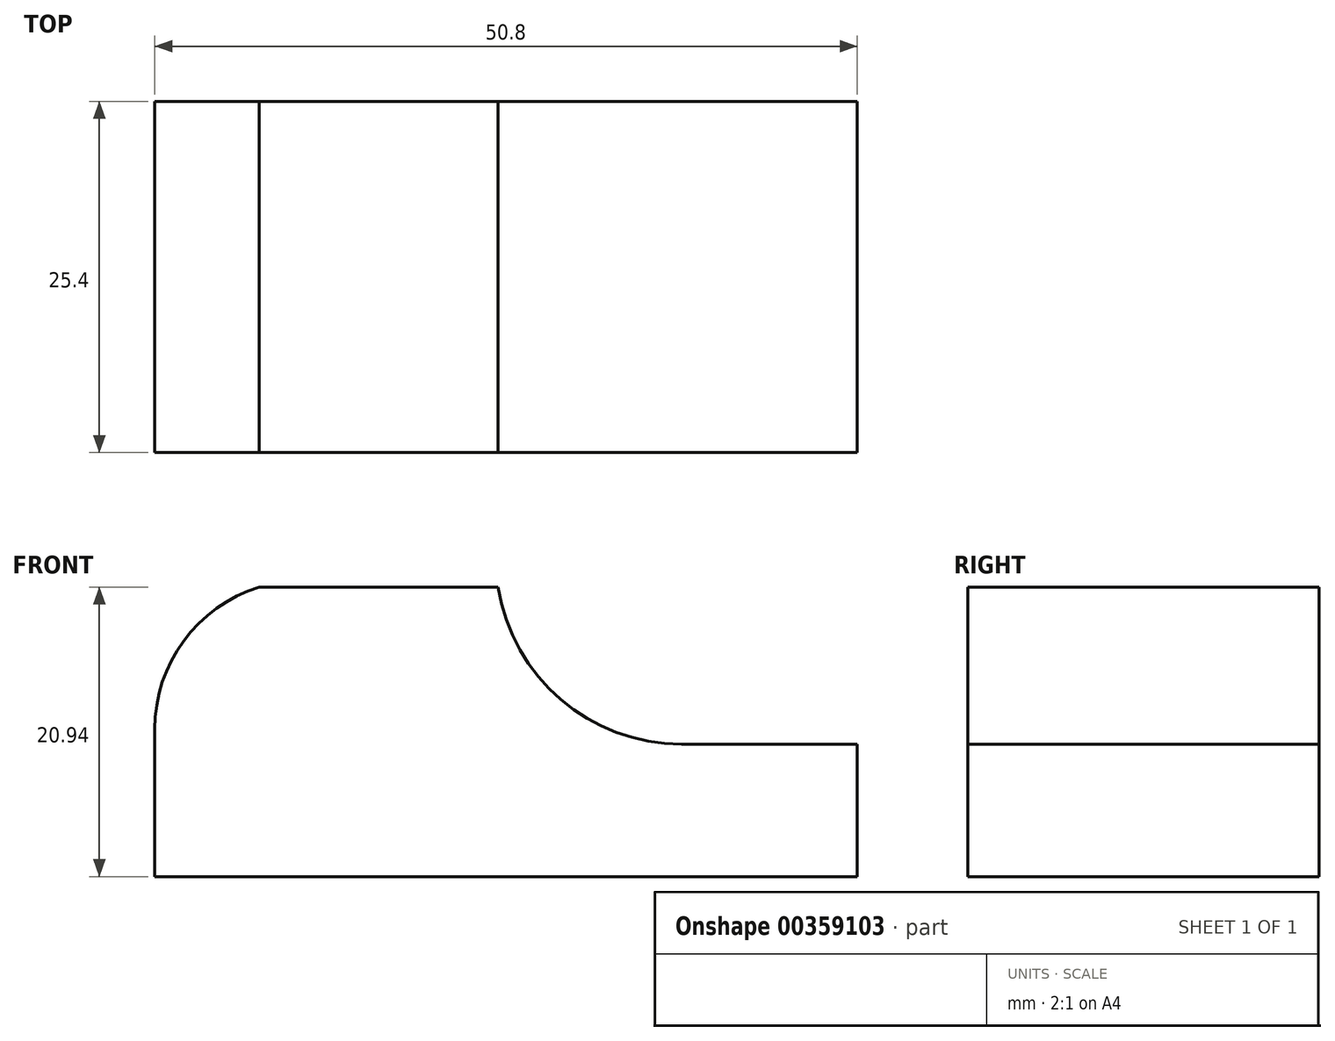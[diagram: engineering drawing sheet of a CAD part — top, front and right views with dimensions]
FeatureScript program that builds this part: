
annotation { "Feature Type Name" : "Feature", "Feature Type Description" : "" }
export const myFeature = defineFeature(function(context is Context, id is Id, definition is map)
    precondition{}
    {
        {
            var Q0;
            Q0=qCreatedBy(makeId("Front.planeOp"),FACE);
            var sketch = newSketch(context, id + "F0", { "sketchPlane" : qUnion([Q0])});
            skLineSegment(sketch, "E0", {"start": v(-56.6, 0) * mm, "end": v(-56.6, 20.94) * mm});
            skLineSegment(sketch, "E1", {"start": v(-56.6, 20.94) * mm, "end": v(-18.5, 20.94) * mm});
            skLineSegment(sketch, "E2", {"start": v(-18.5, 20.94) * mm, "end": v(-18.5, 9.58) * mm});
            skLineSegment(sketch, "E3", {"start": v(-18.5, 9.58) * mm, "end": v(-5.8, 9.58) * mm});
            skLineSegment(sketch, "E4", {"start": v(-5.8, 9.58) * mm, "end": v(-5.8, 0) * mm});
            skLineSegment(sketch, "E5", {"start": v(-5.8, 0) * mm, "end": v(-56.6, 0) * mm});
            skArc(sketch, "E6", {"start": v(-50.79, 20.94) * mm, "mid": v(-55.07, 16.47) * mm, "end": v(-56.6, 10.47) * mm});
            skArc(sketch, "E7", {"start": v(-32.94, 20.94) * mm, "mid": v(-27.68, 12.76) * mm, "end": v(-18.5, 9.58) * mm});
            skSolve(sketch);
        }
        {
            var Q0;
            Q0 = qSketchRegion(id + "F0", true);
            extrude(context, id + "F1", {"entities" : qUnion([Q0]), "depth" : 25.4 * mm});
        }
        {
            var Q0;
            Q0=makeQuery(id+"F1.opExtrude","CAP_FACE",FACE,{"disambiguationData":[OSD([sQuery(id+"F0.wireOp",EDGE,"E0"),sQuery(id+"F0.wireOp",EDGE,"E1"),sQuery(id+"F0.wireOp",EDGE,"E2"),sQuery(id+"F0.wireOp",EDGE,"E3"),sQuery(id+"F0.wireOp",EDGE,"E4"),sQuery(id+"F0.wireOp",EDGE,"E5"),sQuery(id+"F0.wireOp",EDGE,"E6")])],"isStart":false});
            var sketch = newSketch(context, id + "F2", { "sketchPlane" : qUnion([Q0])});
            skArc(sketch, "E8", {"start": v(-49.05, 20.94) * mm, "mid": v(-54.5, 17.05) * mm, "end": v(-56.6, 10.68) * mm});
            skArc(sketch, "E9", {"start": v(-31.76, 20.94) * mm, "mid": v(-27.23, 12.8) * mm, "end": v(-18.5, 9.58) * mm});
            skSolve(sketch);
        }
        {
            var Q0;
            {var subQ0=sQuery(id+"F2.wireOp",EDGE,"E8");Q0=makeQuery(id+"F2.imprint","IMPRINT",FACE,{"disambiguationData":[TD([[makeQuery(id+"F2.imprint","IMPRINT",EDGE,{"derivedFrom":subQ0}),-1.0]])]});}
            var Q1;
            {var subQ0=sQuery(id+"F2.wireOp",EDGE,"E9");Q1=makeQuery(id+"F2.imprint","IMPRINT",FACE,{"disambiguationData":[TD([[makeQuery(id+"F2.imprint","IMPRINT",EDGE,{"derivedFrom":subQ0}),1.0]])]});}
            extrude(context, id + "F3", {"entities" : qUnion([Q0, Q1]), "operationType" : NewBodyOperationType.REMOVE, "oppositeDirection" : true, "depth" : 25.4 * mm});
        }
    });
